# Revit family: Cleverfit Theatre_Hosted_R16
name_source: partatom
category: Lighting Fixtures
revit_build: Autodesk Revit LT 2016 (Build: 20150220_1215(x64)
units: mm (PartAtom-declared; Revit-internal decimal feet)

## family parameters
Cut with Voids When Loaded = No
Host = Face
Light Source = No
Part Type = Normal
Room Calculation Point = No
Round Connector Dimension = Use Diameter
Shared = No

## types (1)
- Cleverfit Theatre_Hosted_R16
    AS2293 = NA – Theatre Mask
    Charging Method = Intelligent current limited constant voltage charger
    Construction = ABS Body with ABS Diffuser and Polycarbonate Clear tamper proof cover.
    Default Elevation = 1219 mm
    Diffuser = Theatre Mask (must specify diffuser combination)
    Height = 215 mm
    IP Rating = IP20
    Lamp = 6 x high intensity, low energy LED, surface mounted onto a replaceable lamp bar - 100,000 hour
    Length = 355 mm
    Mounting = Wall, Ceiling Single-Sided & Ceiling Double-Sided
    Operating Mode = Maintained
    Operating Temperature = 1˚ to 40˚C
    Operating Voltage = 240V 50Hz
    Power Consumption = 2.7W Standby (4.7W during first 16hr charge)
    Testing System = DALI Compatible
    Wattage Comments = Standby
    Width = 80 mm  [stored 0.262467 ft]

note: [stored X ft] marks values corroborated as IEEE doubles in the binary element streams (Revit-internal decimal feet)

## geometry (parser evidence)
native form markers: Sweep x3
no freeform markers — native parametric forms only
